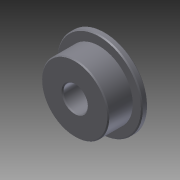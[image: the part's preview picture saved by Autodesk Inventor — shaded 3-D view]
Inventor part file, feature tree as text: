
AUTODESK INVENTOR PART (.ipt)
format: ipt  version: 2014 SP1 (Build 180222100, 222)  size: 109,056 bytes
history: native  units: in
note: dims shown in document units (in); Inventor stores cm internally (conversion verified against a paired STEP export)
features: extrude x2, sketch x1, chamfer x1
ambient origin geometry x8: Origin, YZ Plane, XZ Plane, XY Plane, X Axis, Y Axis, Z Axis, Center Point
bodies: Solid1 (feature_tree)
feature tree (4):
  sketch  "Sketch1"  dims[d0=0.6875in d1=0.875in d2=0.25in d3=0.25in d4=0.0in d5=0.0625in d6=0.0in d7=0.01in d8=0.125in d9=45.0deg]
  extrude  "Extrusion1"  Depth=0.125in
  extrude  "Extrusion2"  Depth=0.25in
  chamfer  "Chamfer1"  Distance=0.25in
